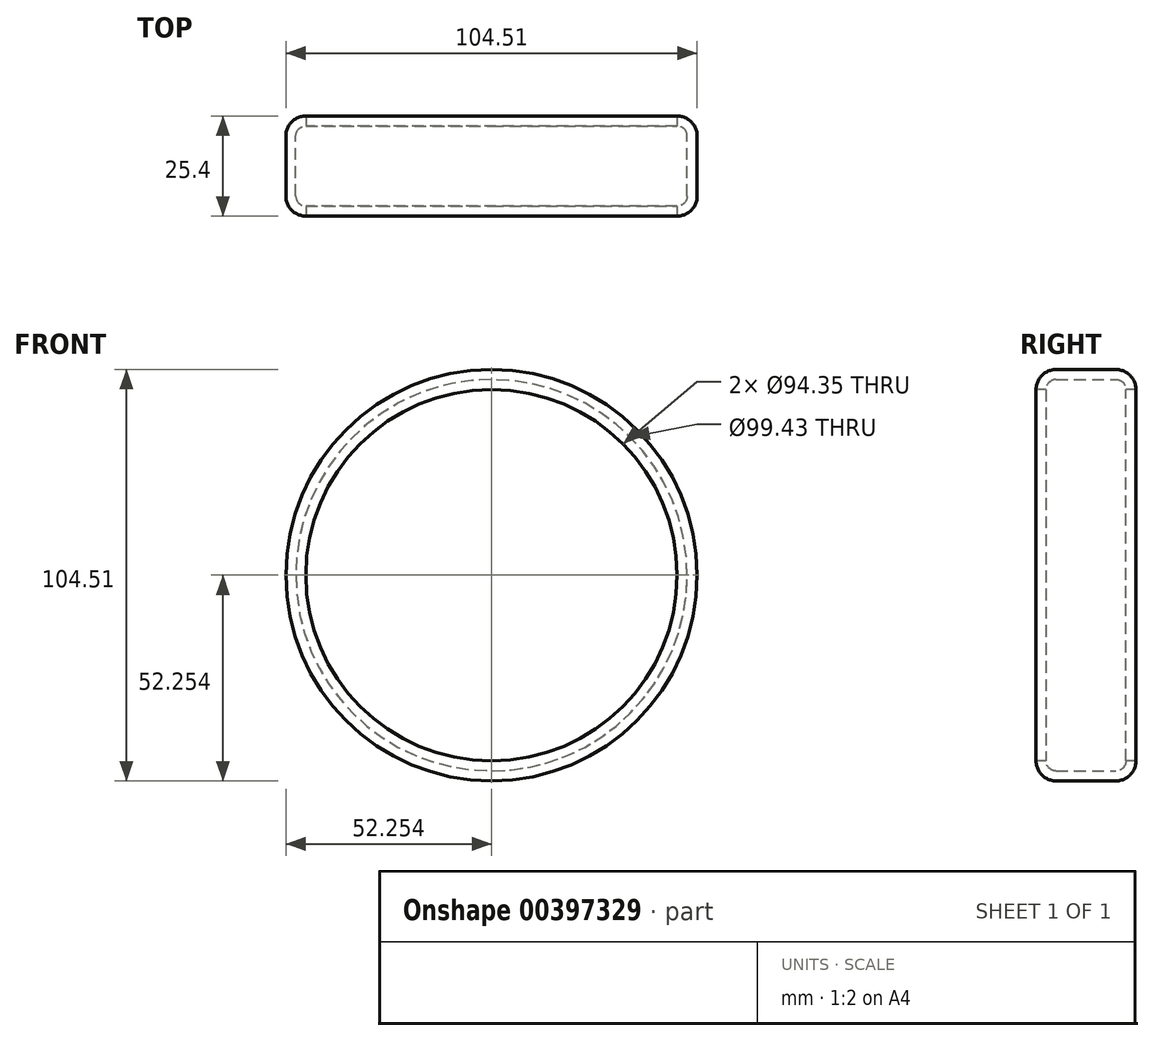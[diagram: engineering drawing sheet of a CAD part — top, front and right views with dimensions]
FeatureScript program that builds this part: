
annotation { "Feature Type Name" : "Feature", "Feature Type Description" : "" }
export const myFeature = defineFeature(function(context is Context, id is Id, definition is map)
    precondition{}
    {
        {
            var Q0;
            Q0=qCreatedBy(makeId("Front.planeOp"),FACE);
            var sketch = newSketch(context, id + "F0", { "sketchPlane" : qUnion([Q0])});
            skCircle(sketch, "E0", {"center": v(-30.6, 74.07) * mm, "radius": 52.26 * mm});
            skSolve(sketch);
        }
        {
            var Q0;
            Q0=makeQuery(id+"F0.imprint","IMPRINT",FACE,{"disambiguationData":[TD([[makeQuery(id+"F0.imprint","IMPRINT",EDGE,{"derivedFrom":sQuery(id+"F0.wireOp",EDGE,"E0")}),1.0]])]});
            extrude(context, id + "F1", {"entities" : qUnion([Q0]), "depth" : 25.4 * mm});
        }
        {
            var Q0;
            Q0=makeQuery(id+"F1.opExtrude","SWEPT_FACE",FACE,{"disambiguationData":[OSD([sQuery(id+"F0.wireOp",EDGE,"E0")])]});
            fillet(context, id + "F2", {"entities" : qUnion([Q0]), "radius" : 5.08 * mm, "tangentPropagation" : true, "allowEdgeOverflow" : false});
        }
        {
            var Q0;
            Q0=makeQuery(id+"F1.opExtrude","CAP_FACE",FACE,{"disambiguationData":[OSD([sQuery(id+"F0.wireOp",EDGE,"E0")])],"isStart":true});
            shell(context, id + "F3", {"entities" : qUnion([Q0]), "thickness" : 2.54 * mm});
        }
        {
            var Q0;
            Q0=makeQuery(id+"F1.opExtrude","CAP_FACE",FACE,{"disambiguationData":[OSD([sQuery(id+"F0.wireOp",EDGE,"E0")])],"isStart":false});
            var Q1;
            {var subQ0=sQuery(id+"F0.wireOp",EDGE,"E0");Q1=makeQuery(id+"F3.opShell","OFFSET_FACE",FACE,{"disambiguationData":[OSD([subQ0]),TDD([makeQuery(id+"F1.opExtrude","CAP_FACE",FACE,{"disambiguationData":[OSD([subQ0])],"isStart":false})])]});}
            shell(context, id + "F4", {"entities" : qUnion([Q0, Q1]), "thickness" : 2.54 * mm});
        }
    });
